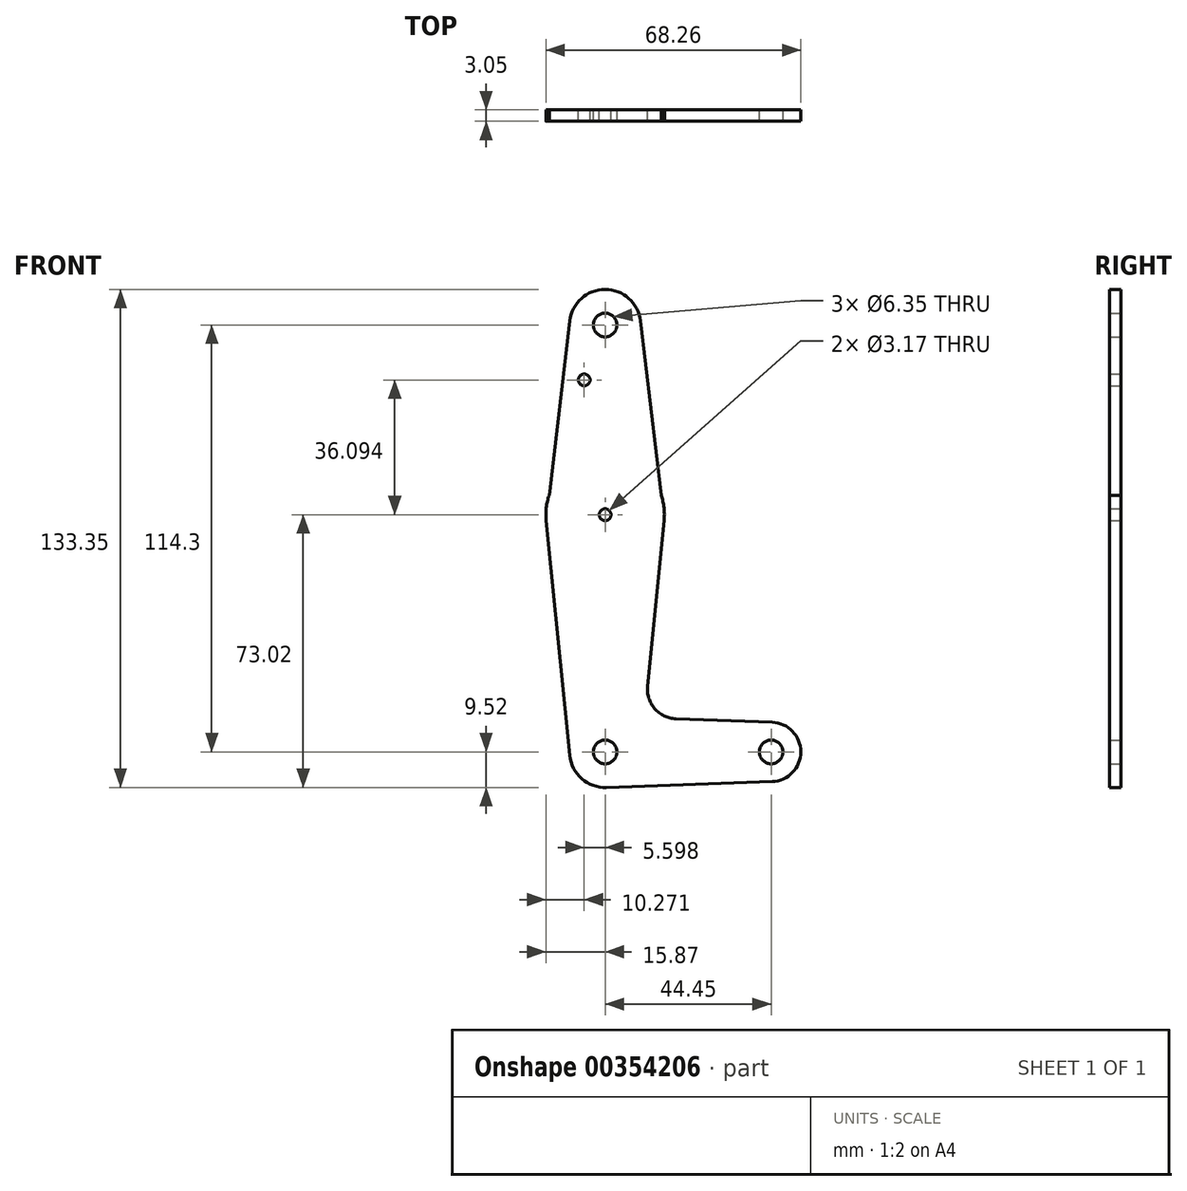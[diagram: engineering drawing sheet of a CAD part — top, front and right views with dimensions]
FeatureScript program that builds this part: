
annotation { "Feature Type Name" : "Feature", "Feature Type Description" : "" }
export const myFeature = defineFeature(function(context is Context, id is Id, definition is map)
    precondition{}
    {
        {
            var Q0;
            Q0=qCreatedBy(makeId("Front.planeOp"),FACE);
            var sketch = newSketch(context, id + "F0", { "sketchPlane" : qUnion([Q0])});
            skLineSegment(sketch, "E0", {"start": v(0, 0) * mm, "end": v(0, 114.3) * mm, "construction": true});
            skLineSegment(sketch, "E1", {"start": v(0, 0) * mm, "end": v(44.45, 0) * mm, "construction": true});
            skCircle(sketch, "E2", {"center": v(0, 0) * mm, "radius": 9.53 * mm});
            skCircle(sketch, "E3", {"center": v(0, 63.5) * mm, "radius": 15.88 * mm});
            skCircle(sketch, "E4", {"center": v(0, 114.3) * mm, "radius": 9.53 * mm});
            skCircle(sketch, "E5", {"center": v(44.45, 0) * mm, "radius": 7.94 * mm});
            skLineSegment(sketch, "E6", {"start": v(-9.46, 115.42) * mm, "end": v(-15.8, 61.91) * mm});
            skLineSegment(sketch, "E7", {"start": v(9.46, 115.42) * mm, "end": v(15.8, 61.91) * mm});
            skLineSegment(sketch, "E8", {"start": v(-15.8, 61.91) * mm, "end": v(-9.48, -0.95) * mm});
            skLineSegment(sketch, "E9", {"start": v(15.8, 61.91) * mm, "end": v(11.34, 17.6) * mm});
            skLineSegment(sketch, "E10", {"start": v(44.73, 7.93) * mm, "end": v(18.97, 8.85) * mm});
            skLineSegment(sketch, "E11", {"start": v(44.73, -7.93) * mm, "end": v(0, -9.53) * mm});
            skCircle(sketch, "E12", {"center": v(0, 63.5) * mm, "radius": 1.59 * mm});
            skCircle(sketch, "E13", {"center": v(0, 0) * mm, "radius": 3.18 * mm});
            skCircle(sketch, "E14", {"center": v(44.45, 0) * mm, "radius": 3.18 * mm});
            skCircle(sketch, "E15", {"center": v(0, 114.3) * mm, "radius": 3.18 * mm});
            skCircle(sketch, "E16", {"center": v(-5.6, 99.6) * mm, "radius": 1.59 * mm});
            skPoint(sketch, "E17.newPointB", {"position": v(0, 9.53) * mm});
            skArc(sketch, "E17.filletArc", {"start": v(11.34, 17.6) * mm, "mid": v(13.26, 11.57) * mm, "end": v(18.97, 8.85) * mm});
            skSolve(sketch);
        }
        {
            var Q0;
            Q0 = qSketchRegion(id + "F0", true);
            extrude(context, id + "F1", {"entities" : qUnion([Q0]), "depth" : 3.05 * mm});
        }
    });
